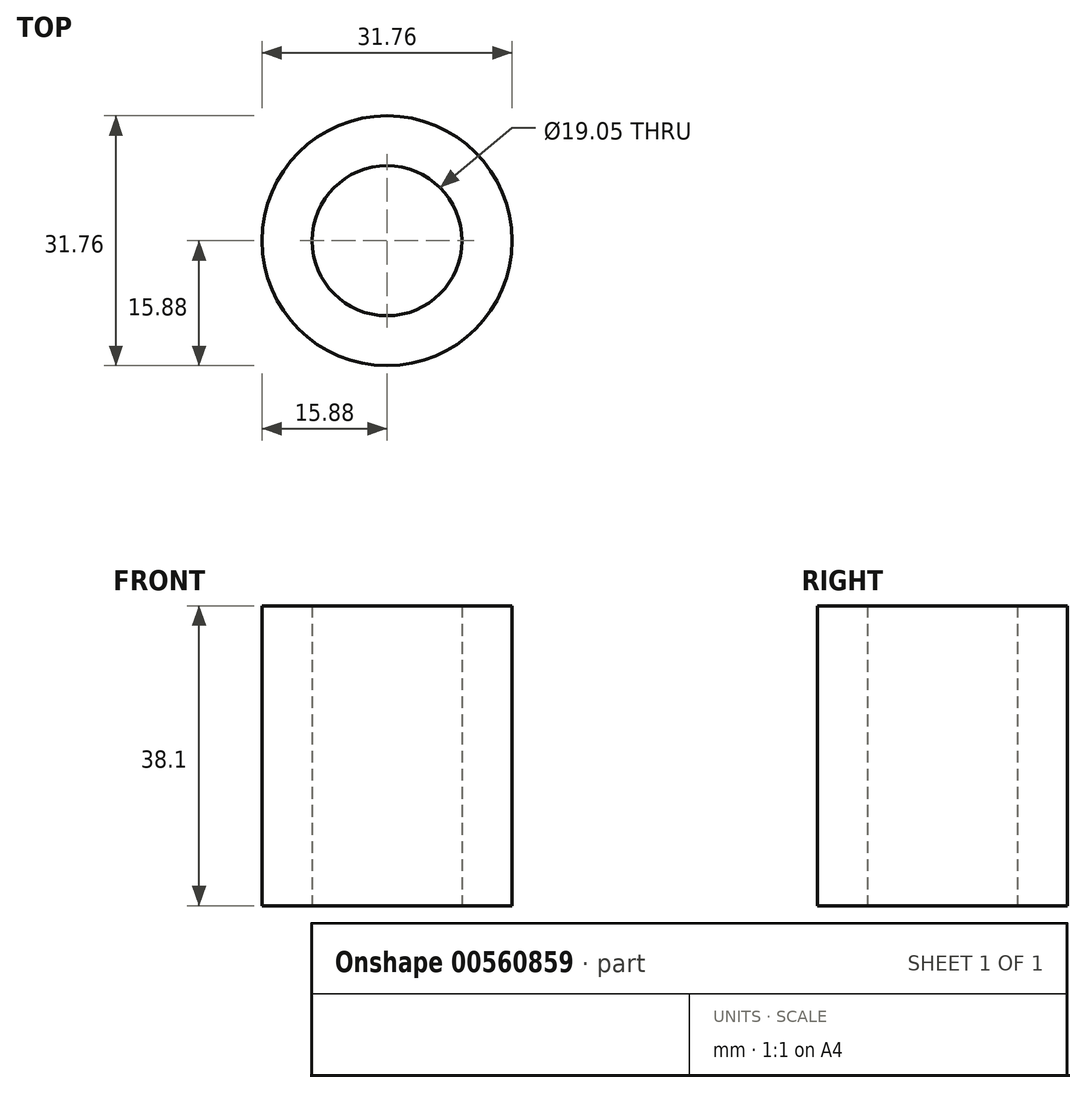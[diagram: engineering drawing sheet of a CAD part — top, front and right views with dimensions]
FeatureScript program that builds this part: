
annotation { "Feature Type Name" : "Feature", "Feature Type Description" : "" }
export const myFeature = defineFeature(function(context is Context, id is Id, definition is map)
    precondition{}
    {
        {
            var Q0;
            Q0=qCreatedBy(makeId("Top.planeOp"),FACE);
            var sketch = newSketch(context, id + "F0", { "sketchPlane" : qUnion([Q0])});
            skCircle(sketch, "E0", {"center": v(0, 0) * mm, "radius": 15.88 * mm});
            skCircle(sketch, "E1", {"center": v(0, 0) * mm, "radius": 9.53 * mm});
            skSolve(sketch);
        }
        {
            var Q0;
            Q0 = qSketchRegion(id + "F0", true);
            extrude(context, id + "F1", {"entities" : qUnion([Q0]), "depth" : 38.1 * mm, "offsetDistance" : 25.4 * mm});
        }
    });
